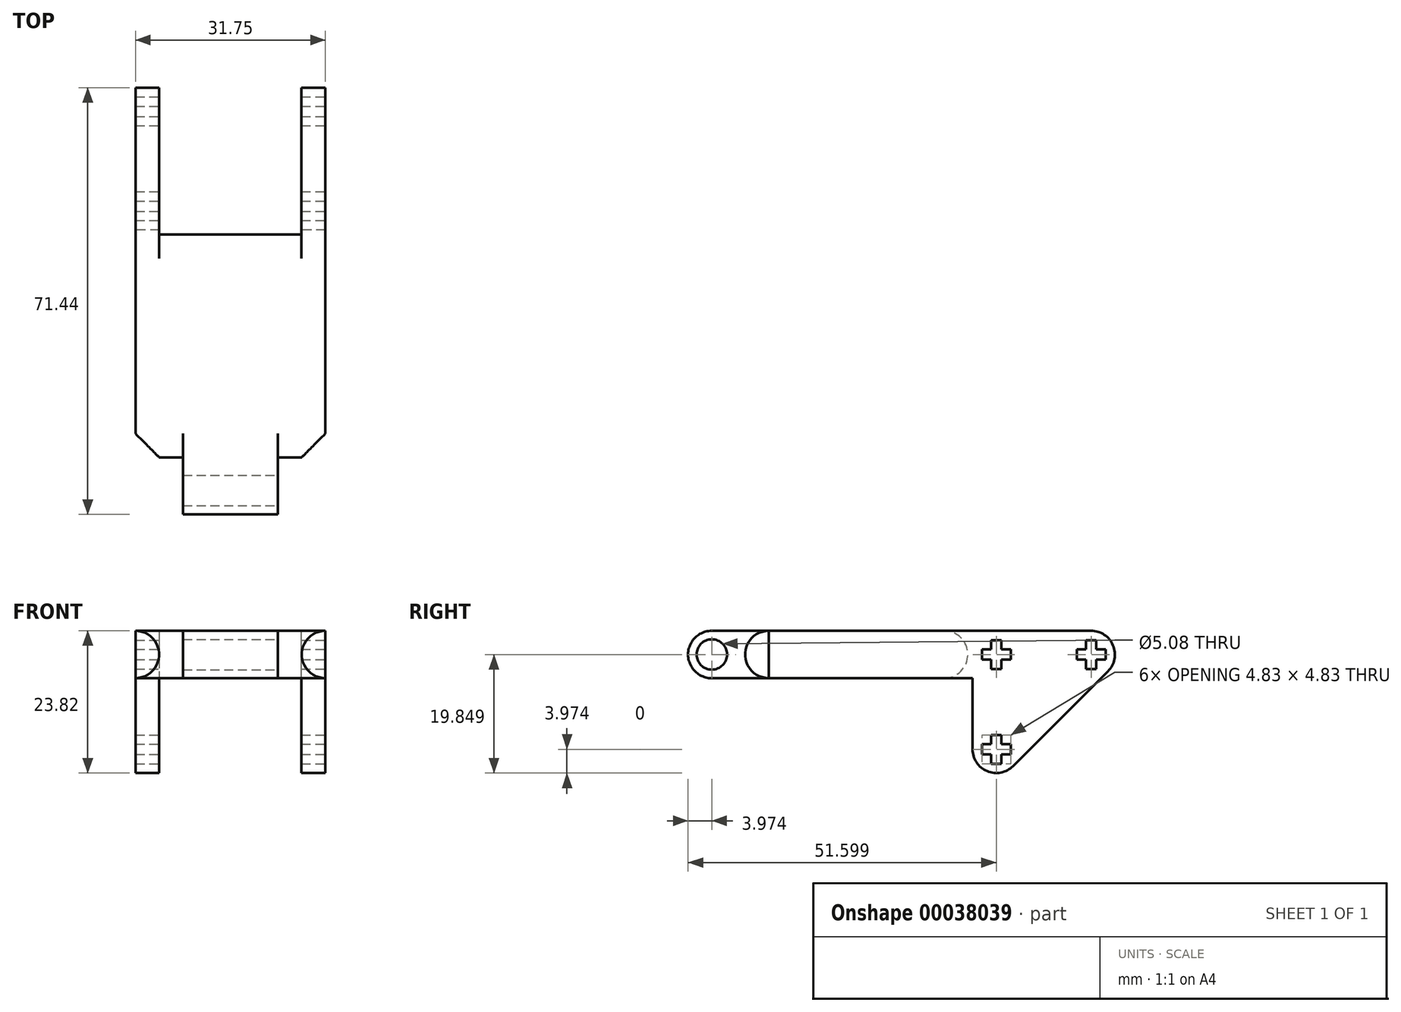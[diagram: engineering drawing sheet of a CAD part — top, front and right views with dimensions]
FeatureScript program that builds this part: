
annotation { "Feature Type Name" : "Feature", "Feature Type Description" : "" }
export const myFeature = defineFeature(function(context is Context, id is Id, definition is map)
    precondition{}
    {
        {
            var Q0;
            Q0=qCreatedBy(makeId("Top.planeOp"),FACE);
            var sketch = newSketch(context, id + "F0", { "sketchPlane" : qUnion([Q0])});
            skLineSegment(sketch, "E0.bottom", {"start": v(0, 0) * mm, "end": v(15.88, 0) * mm, "construction": true});
            skLineSegment(sketch, "E0.top", {"start": v(0, -9.53) * mm, "end": v(15.88, -9.53) * mm});
            skLineSegment(sketch, "E0.left", {"start": v(0, 0) * mm, "end": v(0, -9.53) * mm});
            skLineSegment(sketch, "E0.right", {"start": v(15.88, 0) * mm, "end": v(15.88, -9.53) * mm});
            skLineSegment(sketch, "E1.left", {"start": v(-7.94, 61.91) * mm, "end": v(-7.94, 0) * mm});
            skLineSegment(sketch, "E1.right", {"start": v(23.81, 61.91) * mm, "end": v(23.81, 0) * mm});
            skLineSegment(sketch, "E2", {"start": v(0, 0) * mm, "end": v(-7.94, 0) * mm});
            skLineSegment(sketch, "E3", {"start": v(15.88, 0) * mm, "end": v(23.81, 0) * mm});
            skLineSegment(sketch, "E4", {"start": v(23.81, 61.91) * mm, "end": v(19.84, 61.91) * mm});
            skLineSegment(sketch, "E5", {"start": v(19.84, 61.91) * mm, "end": v(19.84, 37.3) * mm});
            skLineSegment(sketch, "E6", {"start": v(19.84, 37.3) * mm, "end": v(-3.97, 37.3) * mm});
            skLineSegment(sketch, "E7", {"start": v(-3.97, 37.3) * mm, "end": v(-3.97, 61.91) * mm});
            skLineSegment(sketch, "E8", {"start": v(-3.97, 61.91) * mm, "end": v(-7.94, 61.91) * mm});
            skSolve(sketch);
        }
        {
            var Q0;
            Q0 = qSketchRegion(id + "F0", true);
            extrude(context, id + "F1", {"entities" : qUnion([Q0]), "depth" : 7.94 * mm});
        }
        {
            var Q0;
            Q0=makeQuery(id+"F1.opExtrude","CAP_EDGE",EDGE,{"disambiguationData":[OSD([sQuery(id+"F0.wireOp",EDGE,"E3")])],"isStart":false});
            var Q1;
            Q1=makeQuery(id+"F1.opExtrude","CAP_EDGE",EDGE,{"disambiguationData":[OSD([sQuery(id+"F0.wireOp",EDGE,"E3")])],"isStart":true});
            var Q2;
            Q2=makeQuery(id+"F1.opExtrude","CAP_EDGE",EDGE,{"disambiguationData":[OSD([sQuery(id+"F0.wireOp",EDGE,"E0.top")])],"isStart":true});
            var Q3;
            Q3=makeQuery(id+"F1.opExtrude","CAP_EDGE",EDGE,{"disambiguationData":[OSD([sQuery(id+"F0.wireOp",EDGE,"E0.top")])],"isStart":false});
            var Q4;
            Q4=makeQuery(id+"F1.opExtrude","CAP_EDGE",EDGE,{"disambiguationData":[OSD([sQuery(id+"F0.wireOp",EDGE,"E2")])],"isStart":false});
            var Q5;
            Q5=makeQuery(id+"F1.opExtrude","CAP_EDGE",EDGE,{"disambiguationData":[OSD([sQuery(id+"F0.wireOp",EDGE,"E2")])],"isStart":true});
            var Q6;
            Q6=makeQuery(id+"F1.opExtrude","CAP_EDGE",EDGE,{"disambiguationData":[OSD([sQuery(id+"F0.wireOp",EDGE,"E8")])],"isStart":false});
            var Q7;
            Q7=makeQuery(id+"F1.opExtrude","CAP_EDGE",EDGE,{"disambiguationData":[OSD([sQuery(id+"F0.wireOp",EDGE,"E6")])],"isStart":true});
            var Q8;
            Q8=makeQuery(id+"F1.opExtrude","CAP_EDGE",EDGE,{"disambiguationData":[OSD([sQuery(id+"F0.wireOp",EDGE,"E6")])],"isStart":false});
            var Q9;
            Q9=makeQuery(id+"F1.opExtrude","CAP_EDGE",EDGE,{"disambiguationData":[OSD([sQuery(id+"F0.wireOp",EDGE,"E4")])],"isStart":false});
            fillet(context, id + "F2", {"entities" : qUnion([Q0, Q1, Q2, Q3, Q4, Q5, Q6, Q7, Q8, Q9]), "radius" : 3.97 * mm, "tangentPropagation" : true, "allowEdgeOverflow" : false});
        }
        {
            var Q0;
            Q0=makeQuery(id+"F1.opExtrude","CAP_FACE",FACE,{"disambiguationData":[OSD([sQuery(id+"F0.wireOp",EDGE,"E0.top"),sQuery(id+"F0.wireOp",EDGE,"E0.left"),sQuery(id+"F0.wireOp",EDGE,"E0.right"),sQuery(id+"F0.wireOp",EDGE,"E1.bottom"),sQuery(id+"F0.wireOp",EDGE,"E1.left"),sQuery(id+"F0.wireOp",EDGE,"E1.right"),sQuery(id+"F0.wireOp",EDGE,"E2"),sQuery(id+"F0.wireOp",EDGE,"E3")])],"isStart":true});
            var sketch = newSketch(context, id + "F3", { "sketchPlane" : qUnion([Q0])});
            skLineSegment(sketch, "E9.bottom", {"start": v(23.81, -61.91) * mm, "end": v(19.84, -61.91) * mm});
            skLineSegment(sketch, "E9.top", {"start": v(23.81, -38.1) * mm, "end": v(19.84, -38.1) * mm});
            skLineSegment(sketch, "E9.left", {"start": v(23.81, -61.91) * mm, "end": v(23.81, -38.1) * mm});
            skLineSegment(sketch, "E9.right", {"start": v(19.84, -61.91) * mm, "end": v(19.84, -38.1) * mm});
            skLineSegment(sketch, "E10", {"start": v(19.84, -38.1) * mm, "end": v(-3.97, -38.1) * mm, "construction": true});
            skLineSegment(sketch, "E11", {"start": v(7.94, -38.1) * mm, "end": v(7.94, 5.56) * mm, "construction": true});
            skLineSegment(sketch, "E12.bottom", {"start": v(-3.97, -38.1) * mm, "end": v(-7.94, -38.1) * mm});
            skLineSegment(sketch, "E12.top", {"start": v(-3.97, -61.91) * mm, "end": v(-7.94, -61.91) * mm});
            skLineSegment(sketch, "E12.left", {"start": v(-3.97, -38.1) * mm, "end": v(-3.97, -61.91) * mm});
            skLineSegment(sketch, "E12.right", {"start": v(-7.94, -38.1) * mm, "end": v(-7.94, -61.91) * mm});
            skLineSegment(sketch, "E13", {"start": v(-5.95, -38.1) * mm, "end": v(-5.95, -42.07) * mm, "construction": true});
            skLineSegment(sketch, "E14", {"start": v(-3.97, -33.34) * mm, "end": v(-5.95, -33.34) * mm, "construction": true});
            skLineSegment(sketch, "E15", {"start": v(-5.95, -33.34) * mm, "end": v(-5.95, -37.3) * mm, "construction": true});
            skLineSegment(sketch, "E16", {"start": v(-5.95, -37.3) * mm, "end": v(-5.95, -38.1) * mm, "construction": true});
            skSolve(sketch);
        }
        {
            var Q0;
            Q0 = qSketchRegion(id + "F3", true);
            extrude(context, id + "F4", {"entities" : qUnion([Q0]), "operationType" : NewBodyOperationType.ADD, "depth" : 15.88 * mm});
        }
        {
            var Q0;
            Q0=makeQuery(id+"F4.boolean.opBoolean","MERGE",FACE,{"derivedFrom":[makeQuery(id+"F1.opExtrude","SWEPT_FACE",FACE,{"disambiguationData":[OSD([sQuery(id+"F0.wireOp",EDGE,"E1.right")])]}),makeQuery(id+"F4.opExtrude","SWEPT_FACE",FACE,{"disambiguationData":[OSD([sQuery(id+"F3.wireOp",EDGE,"E9.left")])]})]});
            var sketch = newSketch(context, id + "F5", { "sketchPlane" : qUnion([Q0])});
            skLineSegment(sketch, "E17.bottom", {"start": v(61.91, 3.97) * mm, "end": v(38.1, 3.97) * mm, "construction": true});
            skLineSegment(sketch, "E17.top", {"start": v(61.91, -15.88) * mm, "end": v(38.1, -15.88) * mm});
            skLineSegment(sketch, "E17.left", {"start": v(61.91, 3.97) * mm, "end": v(61.91, -15.88) * mm});
            skLineSegment(sketch, "E17.right", {"start": v(38.1, 3.97) * mm, "end": v(38.1, -15.88) * mm});
            skArc(sketch, "E18", {"start": v(38.1, -11.9) * mm, "mid": v(40.55, -15.57) * mm, "end": v(44.88, -14.71) * mm});
            skLineSegment(sketch, "E19", {"start": v(42.07, -11.9) * mm, "end": v(42.07, 3.97) * mm, "construction": true});
            skLineSegment(sketch, "E20.rect.bottom", {"start": v(44.48, -11.06) * mm, "end": v(39.66, -11.06) * mm});
            skLineSegment(sketch, "E20.rect.top", {"start": v(44.48, -12.75) * mm, "end": v(39.66, -12.75) * mm});
            skLineSegment(sketch, "E20.rect.left", {"start": v(44.48, -11.06) * mm, "end": v(44.48, -12.75) * mm});
            skLineSegment(sketch, "E20.rect.right", {"start": v(39.66, -11.06) * mm, "end": v(39.66, -12.75) * mm});
            skLineSegment(sketch, "E21.rect.bottom", {"start": v(41.22, -9.5) * mm, "end": v(42.91, -9.5) * mm});
            skLineSegment(sketch, "E21.rect.top", {"start": v(41.22, -14.32) * mm, "end": v(42.91, -14.32) * mm});
            skLineSegment(sketch, "E21.rect.left", {"start": v(41.22, -9.5) * mm, "end": v(41.22, -14.32) * mm});
            skLineSegment(sketch, "E21.rect.right", {"start": v(42.91, -9.5) * mm, "end": v(42.91, -14.32) * mm});
            skLineSegment(sketch, "E22.rect.bottom", {"start": v(57.1, 6.38) * mm, "end": v(58.79, 6.38) * mm});
            skLineSegment(sketch, "E22.rect.top", {"start": v(57.1, 1.56) * mm, "end": v(58.79, 1.56) * mm});
            skLineSegment(sketch, "E22.rect.left", {"start": v(57.1, 6.38) * mm, "end": v(57.1, 1.56) * mm});
            skLineSegment(sketch, "E22.rect.right", {"start": v(58.79, 6.38) * mm, "end": v(58.79, 1.56) * mm});
            skPoint(sketch, "E22.rect.middle", {"position": v(57.94, 3.97) * mm});
            skLineSegment(sketch, "E23.rect.bottom", {"start": v(55.53, 4.81) * mm, "end": v(60.36, 4.81) * mm});
            skLineSegment(sketch, "E23.rect.top", {"start": v(55.53, 3.12) * mm, "end": v(60.36, 3.12) * mm});
            skLineSegment(sketch, "E23.rect.left", {"start": v(55.53, 4.81) * mm, "end": v(55.53, 3.12) * mm});
            skLineSegment(sketch, "E23.rect.right", {"start": v(60.36, 4.81) * mm, "end": v(60.36, 3.12) * mm});
            skLineSegment(sketch, "E24", {"start": v(37.3, 3.97) * mm, "end": v(42.07, 3.97) * mm, "construction": true});
            skLineSegment(sketch, "E25.rect.bottom", {"start": v(42.91, 1.56) * mm, "end": v(41.22, 1.56) * mm});
            skLineSegment(sketch, "E25.rect.top", {"start": v(42.91, 6.38) * mm, "end": v(41.22, 6.38) * mm});
            skLineSegment(sketch, "E25.rect.left", {"start": v(42.91, 1.56) * mm, "end": v(42.91, 6.38) * mm});
            skLineSegment(sketch, "E25.rect.right", {"start": v(41.22, 1.56) * mm, "end": v(41.22, 6.38) * mm});
            skPoint(sketch, "E25.rect.middle", {"position": v(42.07, 3.97) * mm});
            skLineSegment(sketch, "E26.rect.bottom", {"start": v(44.48, 3.12) * mm, "end": v(39.66, 3.12) * mm});
            skLineSegment(sketch, "E26.rect.top", {"start": v(44.48, 4.81) * mm, "end": v(39.66, 4.81) * mm});
            skLineSegment(sketch, "E26.rect.left", {"start": v(44.48, 3.12) * mm, "end": v(44.48, 4.81) * mm});
            skLineSegment(sketch, "E26.rect.right", {"start": v(39.66, 3.12) * mm, "end": v(39.66, 4.81) * mm});
            skCircle(sketch, "E27", {"center": v(-5.56, 3.97) * mm, "radius": 2.54 * mm});
            skArc(sketch, "E28", {"start": v(60.75, 1.16) * mm, "mid": v(61.61, 2.45) * mm, "end": v(61.91, 3.97) * mm});
            skLineSegment(sketch, "E29", {"start": v(44.88, -14.71) * mm, "end": v(60.75, 1.16) * mm});
            skSolve(sketch);
        }
        {
            var Q0;
            Q0 = qSketchRegion(id + "F5", true);
            var Q1;
            Q1=makeQuery(id+"F4.boolean.opBoolean","MERGE",FACE,{"derivedFrom":[makeQuery(id+"F1.opExtrude","SWEPT_FACE",FACE,{"disambiguationData":[OSD([sQuery(id+"F0.wireOp",EDGE,"E1.left")])]}),makeQuery(id+"F4.opExtrude","SWEPT_FACE",FACE,{"disambiguationData":[OSD([sQuery(id+"F3.wireOp",EDGE,"E12.right")])]})]});
            extrude(context, id + "F6", {"entities" : qUnion([Q0]), "operationType" : NewBodyOperationType.REMOVE, "endBound" : BoundingType.UP_TO_SURFACE, "oppositeDirection" : true, "endBoundEntityFace" : qUnion([Q1]), "depth" : 25.4 * mm});
        }
        {
            var Q0;
            Q0=makeQuery(id+"F1.opExtrude","CAP_FACE",FACE,{"disambiguationData":[OSD([sQuery(id+"F0.wireOp",EDGE,"E0.top"),sQuery(id+"F0.wireOp",EDGE,"E0.left"),sQuery(id+"F0.wireOp",EDGE,"E0.right"),sQuery(id+"F0.wireOp",EDGE,"E1.left"),sQuery(id+"F0.wireOp",EDGE,"E1.right"),sQuery(id+"F0.wireOp",EDGE,"E2"),sQuery(id+"F0.wireOp",EDGE,"E3"),sQuery(id+"F0.wireOp",EDGE,"E4"),sQuery(id+"F0.wireOp",EDGE,"E5"),sQuery(id+"F0.wireOp",EDGE,"E6"),sQuery(id+"F0.wireOp",EDGE,"E7"),sQuery(id+"F0.wireOp",EDGE,"E8")])],"isStart":false});
            var sketch = newSketch(context, id + "F7", { "sketchPlane" : qUnion([Q0])});
            skLineSegment(sketch, "E30.bottom", {"start": v(23.81, 3.97) * mm, "end": v(19.84, 3.97) * mm, "construction": true});
            skLineSegment(sketch, "E30.top", {"start": v(23.81, 0) * mm, "end": v(19.84, 0) * mm});
            skLineSegment(sketch, "E30.left", {"start": v(23.81, 3.97) * mm, "end": v(23.81, 0) * mm});
            skLineSegment(sketch, "E30.right", {"start": v(19.84, 3.97) * mm, "end": v(19.84, 0) * mm, "construction": true});
            skLineSegment(sketch, "E31.bottom", {"start": v(-7.94, 3.97) * mm, "end": v(-3.97, 3.97) * mm, "construction": true});
            skLineSegment(sketch, "E31.top", {"start": v(-7.94, 0) * mm, "end": v(-3.97, 0) * mm});
            skLineSegment(sketch, "E31.left", {"start": v(-7.94, 3.97) * mm, "end": v(-7.94, 0) * mm});
            skLineSegment(sketch, "E31.right", {"start": v(-3.97, 3.97) * mm, "end": v(-3.97, 0) * mm, "construction": true});
            skLineSegment(sketch, "E32", {"start": v(23.81, 3.97) * mm, "end": v(19.84, 0) * mm});
            skLineSegment(sketch, "E33", {"start": v(-7.94, 3.97) * mm, "end": v(-3.97, 0) * mm});
            skSolve(sketch);
        }
        {
            var Q0;
            Q0 = qSketchRegion(id + "F7", true);
            var Q1;
            Q1=makeQuery(id+"F1.opExtrude","CAP_FACE",FACE,{"disambiguationData":[OSD([sQuery(id+"F0.wireOp",EDGE,"E0.top"),sQuery(id+"F0.wireOp",EDGE,"E0.left"),sQuery(id+"F0.wireOp",EDGE,"E0.right"),sQuery(id+"F0.wireOp",EDGE,"E1.left"),sQuery(id+"F0.wireOp",EDGE,"E1.right"),sQuery(id+"F0.wireOp",EDGE,"E2"),sQuery(id+"F0.wireOp",EDGE,"E3"),sQuery(id+"F0.wireOp",EDGE,"E4"),sQuery(id+"F0.wireOp",EDGE,"E5"),sQuery(id+"F0.wireOp",EDGE,"E6"),sQuery(id+"F0.wireOp",EDGE,"E7"),sQuery(id+"F0.wireOp",EDGE,"E8")])],"isStart":true});
            extrude(context, id + "F8", {"entities" : qUnion([Q0]), "operationType" : NewBodyOperationType.REMOVE, "endBound" : BoundingType.UP_TO_SURFACE, "oppositeDirection" : true, "endBoundEntityFace" : qUnion([Q1]), "depth" : 25.4 * mm});
        }
    });
